# Revit family: Spannklaue VA
name_source: partatom
category: HLS-Bauteile
revit_build: Autodesk Revit 2017 (Build: 20190507_1515(x64)
units: mm (PartAtom-declared; Revit-internal decimal feet)

## family parameters
Arbeitsebenenbasiert = Ja
Beim Laden mit Abzugskörper schneiden = Nein
Bemaßung runder Anschluss = Durchmesser verwenden
Gemeinsam genutzt = Nein
Immer vertikal = Nein
Raumberechnungspunkt = Nein
Teiletyp = Normal

## types (1)
- Spannklaue M12 V2A
    Artikelnummer = 0480651
    B = 50 mm  [stored 0.164042 ft]
    B1 = 14 mm  [stored 0.0459318 ft]
    Breite = 50 mm  [stored 0.164042 ft]
    D = 18 mm  [stored 0.0590551 ft]
    EAN = 4250928412775
    Fabrikat = MEFA
    Gewicht = 0.25 kg
    Höhe = 28 mm
    Höhe Profil = 40 mm  [stored 0.131234 ft]
    Klemmdicke = 26 mm
    Kurztext1 = Spannklaue C-Profil 45 V2A
    Kurztext2 = Profilhöhe 40 mm Klemmdicke 26 mm
    L = 73 mm
    Langloch = 14 x 20 mm
    Länge = 727 mm  [stored 2.38517 ft]
    Material = Edelstahl
    Profil = C-Profil
    Profiltyp = 45
    Stärke = 8 mm  [stored 0.0262467 ft]
    Vorgabe-Ansicht = 1219 mm
    für Gewinde = M12
    max. zul. Last = 8.20 kN

note: [stored X ft] marks values corroborated as IEEE doubles in the binary element streams (Revit-internal decimal feet)
